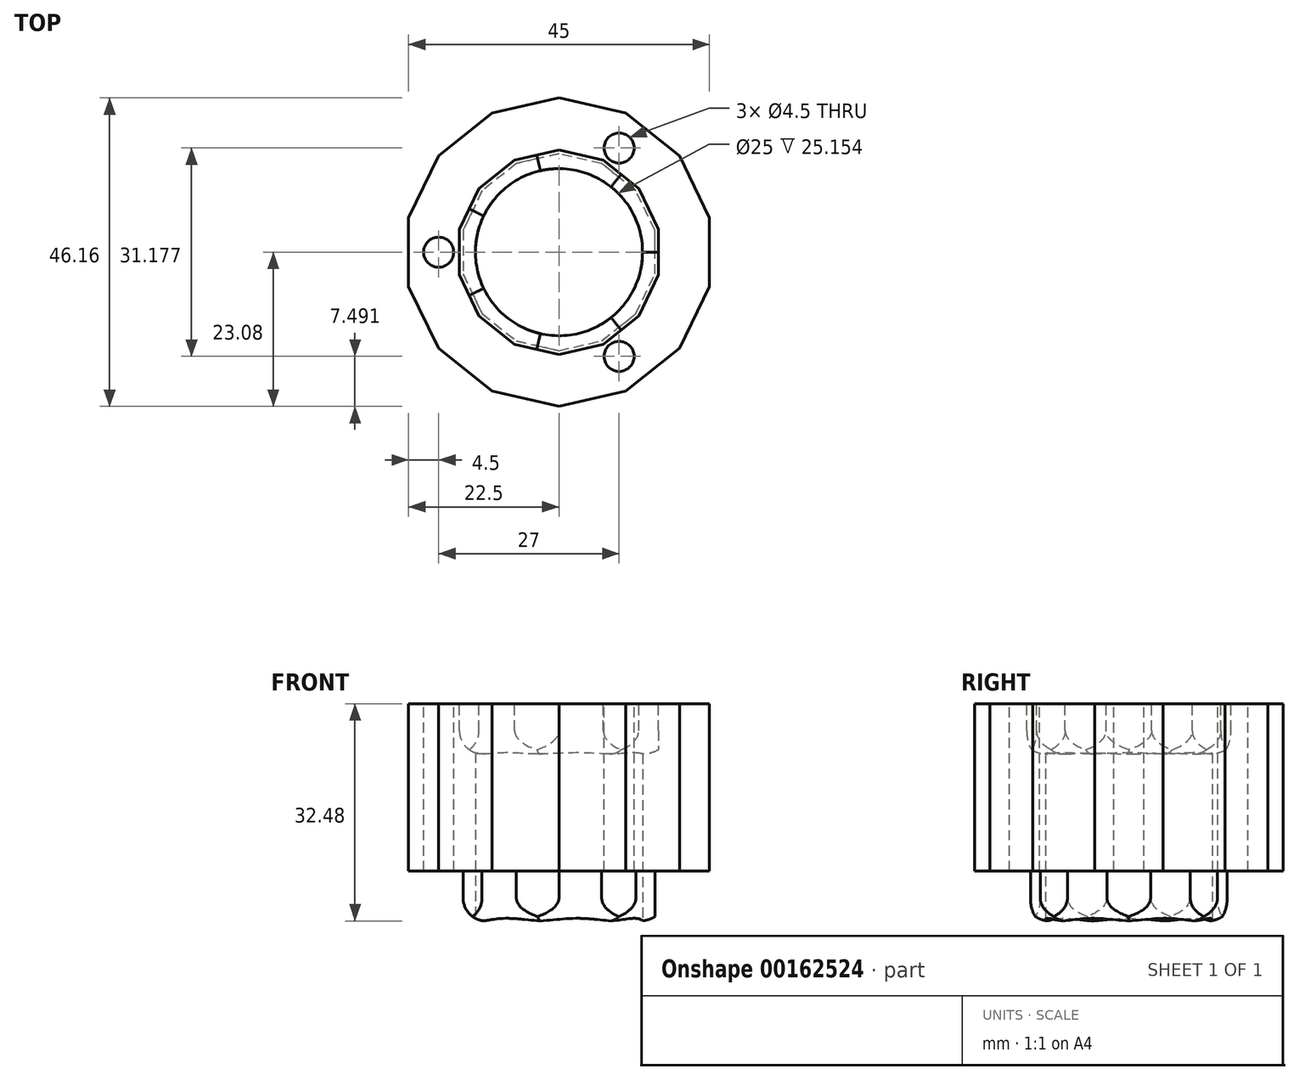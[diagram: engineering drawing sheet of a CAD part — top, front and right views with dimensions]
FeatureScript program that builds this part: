
annotation { "Feature Type Name" : "Feature", "Feature Type Description" : "" }
export const myFeature = defineFeature(function(context is Context, id is Id, definition is map)
    precondition{}
    {
        {
            var Q0;
            Q0=qCreatedBy(makeId("Top.planeOp"),FACE);
            var sketch = newSketch(context, id + "F0", { "sketchPlane" : qUnion([Q0])});
            skCircle(sketch, "E0", {"center": v(0, 0) * mm, "radius": 12.5 * mm});
            skCircle(sketch, "E1.cCircle", {"center": v(0, 0) * mm, "radius": 17.5 * mm, "construction": true});
            skLineSegment(sketch, "E1.0", {"start": v(17.5, 8.43) * mm, "end": v(17.5, -8.43) * mm, "construction": true});
            skLineSegment(sketch, "E1.1", {"start": v(17.5, -8.43) * mm, "end": v(4.32, -18.94) * mm, "construction": true});
            skLineSegment(sketch, "E1.2", {"start": v(4.32, -18.94) * mm, "end": v(-12.11, -15.19) * mm, "construction": true});
            skLineSegment(sketch, "E1.3", {"start": v(-12.11, -15.19) * mm, "end": v(-19.42, 0) * mm, "construction": true});
            skLineSegment(sketch, "E1.4", {"start": v(-19.42, 0) * mm, "end": v(-12.11, 15.19) * mm, "construction": true});
            skLineSegment(sketch, "E1.5", {"start": v(-12.11, 15.19) * mm, "end": v(4.32, 18.94) * mm, "construction": true});
            skLineSegment(sketch, "E1.6", {"start": v(4.32, 18.94) * mm, "end": v(17.5, 8.43) * mm, "construction": true});
            skPoint(sketch, "E1.0.midPoint", {"position": v(17.5, 0) * mm});
            skArc(sketch, "E2", {"start": v(7.16, 16.67) * mm, "mid": v(13.9, 17.43) * mm, "end": v(14.66, 10.69) * mm, "construction": true});
            skArc(sketch, "E3", {"start": v(0.79, 18.13) * mm, "mid": v(-4.96, 21.74) * mm, "end": v(-8.57, 16) * mm, "construction": true});
            skArc(sketch, "E4", {"start": v(-13.68, 11.92) * mm, "mid": v(-20.1, 9.68) * mm, "end": v(-17.85, 3.27) * mm, "construction": true});
            skArc(sketch, "E5", {"start": v(-17.85, -3.27) * mm, "mid": v(-20.1, -9.68) * mm, "end": v(-13.68, -11.92) * mm, "construction": true});
            skArc(sketch, "E6", {"start": v(-8.57, -16) * mm, "mid": v(-4.96, -21.74) * mm, "end": v(0.79, -18.13) * mm, "construction": true});
            skArc(sketch, "E7", {"start": v(14.66, -10.69) * mm, "mid": v(13.9, -17.43) * mm, "end": v(7.16, -16.67) * mm, "construction": true});
            skCircle(sketch, "E8.cCircle", {"center": v(0, 0) * mm, "radius": 22.5 * mm, "construction": true});
            skLineSegment(sketch, "E8.0", {"start": v(22.5, 5.14) * mm, "end": v(22.5, -5.14) * mm});
            skLineSegment(sketch, "E8.1", {"start": v(22.5, -5.14) * mm, "end": v(18.04, -14.39) * mm});
            skLineSegment(sketch, "E8.2", {"start": v(18.04, -14.39) * mm, "end": v(10.01, -20.8) * mm});
            skLineSegment(sketch, "E8.3", {"start": v(10.01, -20.8) * mm, "end": v(0, -23.08) * mm});
            skLineSegment(sketch, "E8.4", {"start": v(0, -23.08) * mm, "end": v(-10.01, -20.8) * mm});
            skLineSegment(sketch, "E8.5", {"start": v(-10.01, -20.8) * mm, "end": v(-18.04, -14.39) * mm});
            skLineSegment(sketch, "E8.6", {"start": v(-18.04, -14.39) * mm, "end": v(-22.5, -5.14) * mm});
            skLineSegment(sketch, "E8.7", {"start": v(-22.5, -5.14) * mm, "end": v(-22.5, 5.14) * mm});
            skLineSegment(sketch, "E8.8", {"start": v(-22.5, 5.14) * mm, "end": v(-18.04, 14.39) * mm});
            skLineSegment(sketch, "E8.9", {"start": v(-18.04, 14.39) * mm, "end": v(-10.01, 20.8) * mm});
            skLineSegment(sketch, "E8.10", {"start": v(-10.01, 20.8) * mm, "end": v(0, 23.08) * mm});
            skLineSegment(sketch, "E8.11", {"start": v(0, 23.08) * mm, "end": v(10.01, 20.8) * mm});
            skLineSegment(sketch, "E8.12", {"start": v(10.01, 20.8) * mm, "end": v(18.04, 14.39) * mm});
            skLineSegment(sketch, "E8.13", {"start": v(18.04, 14.39) * mm, "end": v(22.5, 5.14) * mm});
            skPoint(sketch, "E8.0.midPoint", {"position": v(22.5, 0) * mm});
            skSolve(sketch);
        }
        {
            var Q0;
            Q0=qSketchRegion(id+"F0",true);
            extrude(context, id + "F1", {"entities" : qUnion([Q0]), "endBound" : BoundingType.SYMMETRIC, "depth" : 25 * mm, "offsetDistance" : 25 * mm});
        }
        {
            var Q0;
            Q0=makeQuery(id+"F1.opExtrude","CAP_FACE",FACE,{"disambiguationData":[OSD([sQuery(id+"F0.wireOp",EDGE,"E0"),sQuery(id+"F0.wireOp",EDGE,"E1.0"),sQuery(id+"F0.wireOp",EDGE,"E1.1"),sQuery(id+"F0.wireOp",EDGE,"E1.2"),sQuery(id+"F0.wireOp",EDGE,"E1.3"),sQuery(id+"F0.wireOp",EDGE,"E1.4"),sQuery(id+"F0.wireOp",EDGE,"E1.5"),sQuery(id+"F0.wireOp",EDGE,"E1.6"),sQuery(id+"F0.wireOp",EDGE,"E2"),sQuery(id+"F0.wireOp",EDGE,"E3"),sQuery(id+"F0.wireOp",EDGE,"E4"),sQuery(id+"F0.wireOp",EDGE,"E5"),sQuery(id+"F0.wireOp",EDGE,"E6"),sQuery(id+"F0.wireOp",EDGE,"E7")])],"isStart":false});
            var sketch = newSketch(context, id + "F2", { "sketchPlane" : qUnion([Q0])});
            skLineSegment(sketch, "E9", {"start": v(0, 0) * mm, "end": v(11.38, 19.7) * mm, "construction": true});
            skCircle(sketch, "E10", {"center": v(9, 15.59) * mm, "radius": 2.25 * mm});
            skCircle(sketch, "E11.1.0", {"center": v(-18, 0) * mm, "radius": 2.25 * mm});
            skCircle(sketch, "E11.2.0", {"center": v(9, -15.59) * mm, "radius": 2.25 * mm});
            skPoint(sketch, "E11.center", {"position": v(0, 0) * mm});
            skSolve(sketch);
        }
        {
            var Q0;
            Q0=qSketchRegion(id+"F2",true);
            extrude(context, id + "F3", {"entities" : qUnion([Q0]), "operationType" : NewBodyOperationType.REMOVE, "oppositeDirection" : true, "depth" : 25 * mm, "offsetDistance" : 25 * mm});
        }
        {
            var Q0;
            Q0=makeQuery(id+"F1.opExtrude","CAP_FACE",FACE,{"disambiguationData":[OSD([sQuery(id+"F0.wireOp",EDGE,"E0"),sQuery(id+"F0.wireOp",EDGE,"E1.0"),sQuery(id+"F0.wireOp",EDGE,"E1.1"),sQuery(id+"F0.wireOp",EDGE,"E1.2"),sQuery(id+"F0.wireOp",EDGE,"E1.3"),sQuery(id+"F0.wireOp",EDGE,"E1.4"),sQuery(id+"F0.wireOp",EDGE,"E1.5"),sQuery(id+"F0.wireOp",EDGE,"E1.6"),sQuery(id+"F0.wireOp",EDGE,"E2"),sQuery(id+"F0.wireOp",EDGE,"E3"),sQuery(id+"F0.wireOp",EDGE,"E4"),sQuery(id+"F0.wireOp",EDGE,"E5"),sQuery(id+"F0.wireOp",EDGE,"E6"),sQuery(id+"F0.wireOp",EDGE,"E7")])],"isStart":false});
            var sketch = newSketch(context, id + "F4", { "sketchPlane" : qUnion([Q0])});
            skCircle(sketch, "E12", {"center": v(0, 0) * mm, "radius": 12.5 * mm});
            skCircle(sketch, "E13.cCircle", {"center": v(0, 0) * mm, "radius": 14.9 * mm, "construction": true});
            skLineSegment(sketch, "E13.0", {"start": v(14.9, 3.4) * mm, "end": v(14.9, -3.4) * mm});
            skLineSegment(sketch, "E13.1", {"start": v(14.9, -3.4) * mm, "end": v(11.95, -9.53) * mm});
            skLineSegment(sketch, "E13.2", {"start": v(11.95, -9.53) * mm, "end": v(6.63, -13.77) * mm});
            skLineSegment(sketch, "E13.3", {"start": v(6.63, -13.77) * mm, "end": v(0, -15.28) * mm});
            skLineSegment(sketch, "E13.4", {"start": v(0, -15.28) * mm, "end": v(-6.63, -13.77) * mm});
            skLineSegment(sketch, "E13.5", {"start": v(-6.63, -13.77) * mm, "end": v(-11.95, -9.53) * mm});
            skLineSegment(sketch, "E13.6", {"start": v(-11.95, -9.53) * mm, "end": v(-14.9, -3.4) * mm});
            skLineSegment(sketch, "E13.7", {"start": v(-14.9, -3.4) * mm, "end": v(-14.9, 3.4) * mm});
            skLineSegment(sketch, "E13.8", {"start": v(-14.9, 3.4) * mm, "end": v(-11.95, 9.53) * mm});
            skLineSegment(sketch, "E13.9", {"start": v(-11.95, 9.53) * mm, "end": v(-6.63, 13.77) * mm});
            skLineSegment(sketch, "E13.10", {"start": v(-6.63, 13.77) * mm, "end": v(0, 15.28) * mm});
            skLineSegment(sketch, "E13.11", {"start": v(0, 15.28) * mm, "end": v(6.63, 13.77) * mm});
            skLineSegment(sketch, "E13.12", {"start": v(6.63, 13.77) * mm, "end": v(11.95, 9.53) * mm});
            skLineSegment(sketch, "E13.13", {"start": v(11.95, 9.53) * mm, "end": v(14.9, 3.4) * mm});
            skPoint(sketch, "E13.0.midPoint", {"position": v(14.9, 0) * mm});
            skSolve(sketch);
        }
        {
            var Q0;
            Q0=qSketchRegion(id+"F4",true);
            extrude(context, id + "F5", {"entities" : qUnion([Q0]), "operationType" : NewBodyOperationType.REMOVE, "oppositeDirection" : true, "depth" : 7.5 * mm, "offsetDistance" : 25 * mm});
        }
        {
            var Q0;
            Q0=makeQuery(id+"F1.opExtrude","CAP_FACE",FACE,{"disambiguationData":[OSD([sQuery(id+"F0.wireOp",EDGE,"E0"),sQuery(id+"F0.wireOp",EDGE,"E1.0"),sQuery(id+"F0.wireOp",EDGE,"E1.1"),sQuery(id+"F0.wireOp",EDGE,"E1.2"),sQuery(id+"F0.wireOp",EDGE,"E1.3"),sQuery(id+"F0.wireOp",EDGE,"E1.4"),sQuery(id+"F0.wireOp",EDGE,"E1.5"),sQuery(id+"F0.wireOp",EDGE,"E1.6"),sQuery(id+"F0.wireOp",EDGE,"E2"),sQuery(id+"F0.wireOp",EDGE,"E3"),sQuery(id+"F0.wireOp",EDGE,"E4"),sQuery(id+"F0.wireOp",EDGE,"E5"),sQuery(id+"F0.wireOp",EDGE,"E6"),sQuery(id+"F0.wireOp",EDGE,"E7")])],"isStart":true});
            var sketch = newSketch(context, id + "F6", { "sketchPlane" : qUnion([Q0])});
            skCircle(sketch, "E14", {"center": v(0, 0) * mm, "radius": 12.5 * mm});
            skCircle(sketch, "E15.cCircle", {"center": v(0, 0) * mm, "radius": 14.35 * mm, "construction": true});
            skLineSegment(sketch, "E15.0", {"start": v(14.35, 3.28) * mm, "end": v(14.35, -3.28) * mm});
            skLineSegment(sketch, "E15.1", {"start": v(14.35, -3.28) * mm, "end": v(11.5, -9.18) * mm});
            skLineSegment(sketch, "E15.2", {"start": v(11.5, -9.18) * mm, "end": v(6.39, -13.26) * mm});
            skLineSegment(sketch, "E15.3", {"start": v(6.39, -13.26) * mm, "end": v(0, -14.72) * mm});
            skLineSegment(sketch, "E15.4", {"start": v(0, -14.72) * mm, "end": v(-6.39, -13.26) * mm});
            skLineSegment(sketch, "E15.5", {"start": v(-6.39, -13.26) * mm, "end": v(-11.5, -9.18) * mm});
            skLineSegment(sketch, "E15.6", {"start": v(-11.5, -9.18) * mm, "end": v(-14.35, -3.28) * mm});
            skLineSegment(sketch, "E15.7", {"start": v(-14.35, -3.28) * mm, "end": v(-14.35, 3.28) * mm});
            skLineSegment(sketch, "E15.8", {"start": v(-14.35, 3.28) * mm, "end": v(-11.5, 9.18) * mm});
            skLineSegment(sketch, "E15.9", {"start": v(-11.5, 9.18) * mm, "end": v(-6.39, 13.26) * mm});
            skLineSegment(sketch, "E15.10", {"start": v(-6.39, 13.26) * mm, "end": v(0, 14.72) * mm});
            skLineSegment(sketch, "E15.11", {"start": v(0, 14.72) * mm, "end": v(6.39, 13.26) * mm});
            skLineSegment(sketch, "E15.12", {"start": v(6.39, 13.26) * mm, "end": v(11.5, 9.18) * mm});
            skLineSegment(sketch, "E15.13", {"start": v(11.5, 9.18) * mm, "end": v(14.35, 3.28) * mm});
            skPoint(sketch, "E15.0.midPoint", {"position": v(14.35, 0) * mm});
            skSolve(sketch);
        }
        {
            var Q0;
            Q0=qSketchRegion(id+"F6",true);
            extrude(context, id + "F7", {"entities" : qUnion([Q0]), "operationType" : NewBodyOperationType.ADD, "depth" : 7.5 * mm, "offsetDistance" : 25 * mm});
        }
        {
            var Q0;
            Q0=makeQuery(id+"F5.boolean.opBoolean","COPY",EDGE,{"derivedFrom":makeQuery(id+"F5.opExtrude","CAP_EDGE",EDGE,{"disambiguationData":[OSD([sQuery(id+"F4.wireOp",EDGE,"E13.9")])],"isStart":false})});
            var Q1;
            Q1=makeQuery(id+"F5.boolean.opBoolean","COPY",EDGE,{"derivedFrom":makeQuery(id+"F5.opExtrude","CAP_EDGE",EDGE,{"disambiguationData":[OSD([sQuery(id+"F4.wireOp",EDGE,"E13.7")])],"isStart":false})});
            var Q2;
            Q2=makeQuery(id+"F5.boolean.opBoolean","COPY",EDGE,{"derivedFrom":makeQuery(id+"F5.opExtrude","CAP_EDGE",EDGE,{"disambiguationData":[OSD([sQuery(id+"F4.wireOp",EDGE,"E13.5")])],"isStart":false})});
            var Q3;
            Q3=makeQuery(id+"F5.boolean.opBoolean","COPY",EDGE,{"derivedFrom":makeQuery(id+"F5.opExtrude","CAP_EDGE",EDGE,{"disambiguationData":[OSD([sQuery(id+"F4.wireOp",EDGE,"E13.3")])],"isStart":false})});
            var Q4;
            Q4=makeQuery(id+"F5.boolean.opBoolean","COPY",EDGE,{"derivedFrom":makeQuery(id+"F5.opExtrude","CAP_EDGE",EDGE,{"disambiguationData":[OSD([sQuery(id+"F4.wireOp",EDGE,"E13.1")])],"isStart":false})});
            var Q5;
            Q5=makeQuery(id+"F5.boolean.opBoolean","COPY",EDGE,{"derivedFrom":makeQuery(id+"F5.opExtrude","CAP_EDGE",EDGE,{"disambiguationData":[OSD([sQuery(id+"F4.wireOp",EDGE,"E13.13")])],"isStart":false})});
            var Q6;
            Q6=makeQuery(id+"F5.boolean.opBoolean","COPY",EDGE,{"derivedFrom":makeQuery(id+"F5.opExtrude","CAP_EDGE",EDGE,{"disambiguationData":[OSD([sQuery(id+"F4.wireOp",EDGE,"E13.11")])],"isStart":false})});
            fillet(context, id + "F8", {"entities" : qUnion([Q0, Q1, Q2, Q3, Q4, Q5, Q6]), "radius" : 3.5 * mm, "tangentPropagation" : true, "allowEdgeOverflow" : false});
        }
        {
            var Q0;
            Q0=makeQuery(id+"F7.opExtrude","CAP_EDGE",EDGE,{"disambiguationData":[OSD([sQuery(id+"F6.wireOp",EDGE,"E15.1")])],"isStart":false});
            var Q1;
            Q1=makeQuery(id+"F7.opExtrude","CAP_EDGE",EDGE,{"disambiguationData":[OSD([sQuery(id+"F6.wireOp",EDGE,"E15.3")])],"isStart":false});
            var Q2;
            Q2=makeQuery(id+"F7.opExtrude","CAP_EDGE",EDGE,{"disambiguationData":[OSD([sQuery(id+"F6.wireOp",EDGE,"E15.5")])],"isStart":false});
            var Q3;
            Q3=makeQuery(id+"F7.opExtrude","CAP_EDGE",EDGE,{"disambiguationData":[OSD([sQuery(id+"F6.wireOp",EDGE,"E15.7")])],"isStart":false});
            var Q4;
            Q4=makeQuery(id+"F7.opExtrude","CAP_EDGE",EDGE,{"disambiguationData":[OSD([sQuery(id+"F6.wireOp",EDGE,"E15.9")])],"isStart":false});
            var Q5;
            Q5=makeQuery(id+"F7.opExtrude","CAP_EDGE",EDGE,{"disambiguationData":[OSD([sQuery(id+"F6.wireOp",EDGE,"E15.11")])],"isStart":false});
            var Q6;
            Q6=makeQuery(id+"F7.opExtrude","CAP_EDGE",EDGE,{"disambiguationData":[OSD([sQuery(id+"F6.wireOp",EDGE,"E15.13")])],"isStart":false});
            fillet(context, id + "F9", {"entities" : qUnion([Q0, Q1, Q2, Q3, Q4, Q5, Q6]), "radius" : 3.5 * mm, "allowEdgeOverflow" : false});
        }
    });
